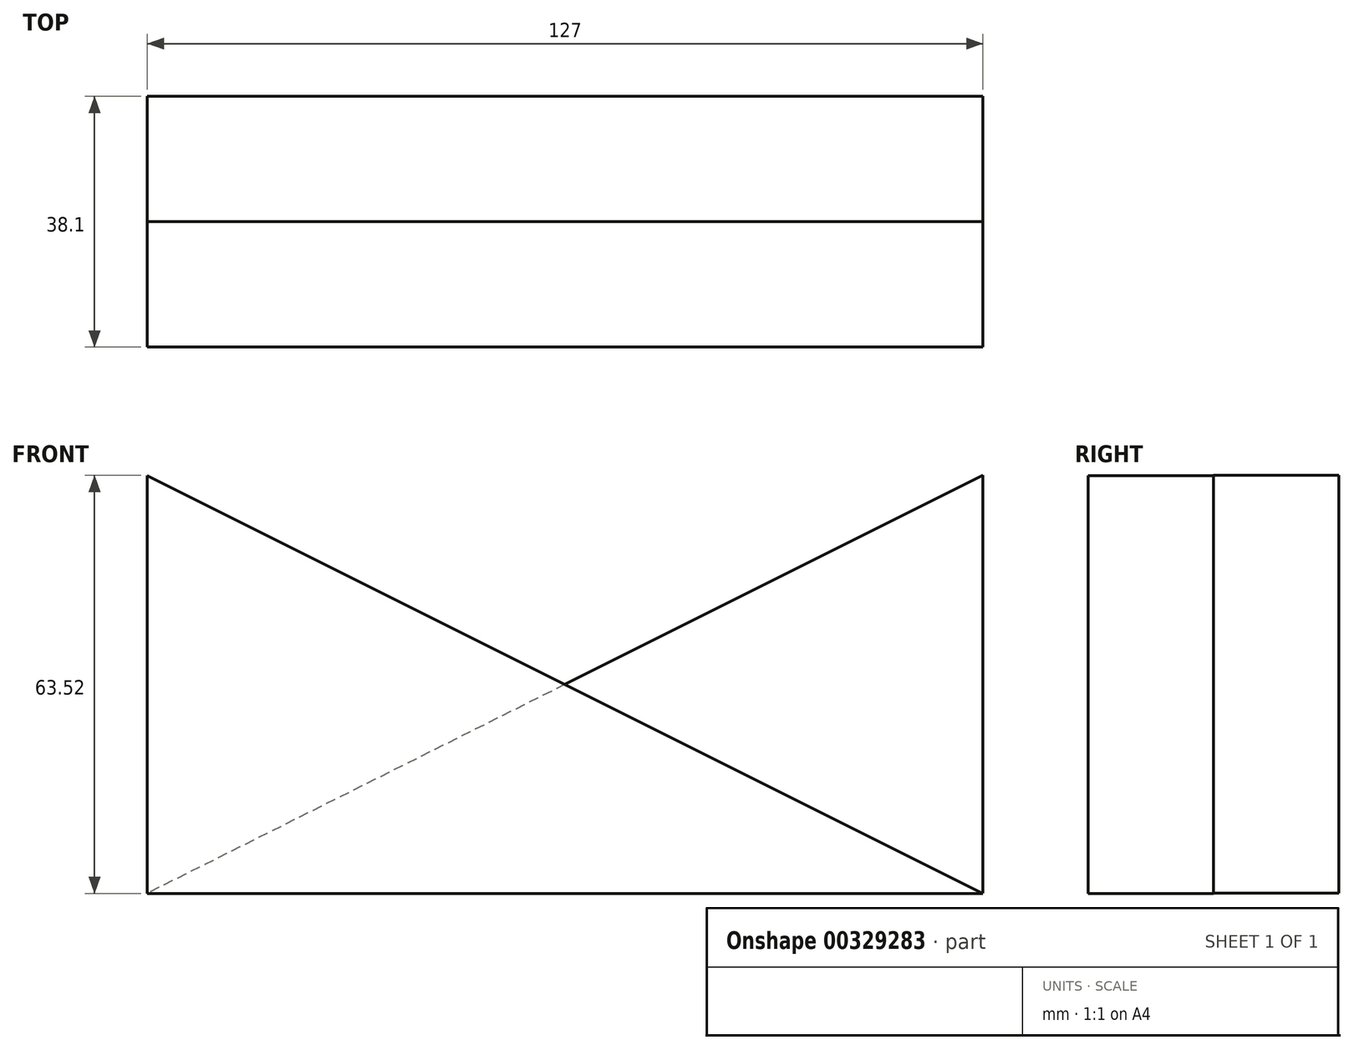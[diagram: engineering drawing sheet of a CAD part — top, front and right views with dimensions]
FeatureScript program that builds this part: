
annotation { "Feature Type Name" : "Feature", "Feature Type Description" : "" }
export const myFeature = defineFeature(function(context is Context, id is Id, definition is map)
    precondition{}
    {
        {
            var Q0;
            Q0=qCreatedBy(makeId("Front.planeOp"),FACE);
            var sketch = newSketch(context, id + "F0", { "sketchPlane" : qUnion([Q0])});
            skLineSegment(sketch, "E0", {"start": v(-66.85, -17.93) * mm, "end": v(60.15, -17.93) * mm});
            skLineSegment(sketch, "E1", {"start": v(-66.85, -17.93) * mm, "end": v(-66.85, 45.57) * mm});
            skLineSegment(sketch, "E2", {"start": v(-66.85, 45.57) * mm, "end": v(60.15, -17.93) * mm});
            skSolve(sketch);
        }
        {
            var Q0;
            Q0 = qSketchRegion(id + "F0", true);
            extrude(context, id + "F1", {"entities" : qUnion([Q0]), "depth" : 19.05 * mm});
        }
        {
            var Q0;
            Q0=qCreatedBy(makeId("Front.planeOp"),FACE);
            var sketch = newSketch(context, id + "F2", { "sketchPlane" : qUnion([Q0])});
            skLineSegment(sketch, "E3", {"start": v(-66.85, -17.91) * mm, "end": v(60.15, -17.91) * mm});
            skLineSegment(sketch, "E4", {"start": v(60.15, -17.91) * mm, "end": v(60.15, 45.59) * mm});
            skLineSegment(sketch, "E5", {"start": v(60.15, 45.59) * mm, "end": v(-66.85, -17.91) * mm});
            skSolve(sketch);
        }
        {
            var Q0;
            Q0 = qSketchRegion(id + "F2", true);
            extrude(context, id + "F3", {"entities" : qUnion([Q0]), "operationType" : NewBodyOperationType.ADD, "oppositeDirection" : true, "depth" : 19.05 * mm});
        }
    });
